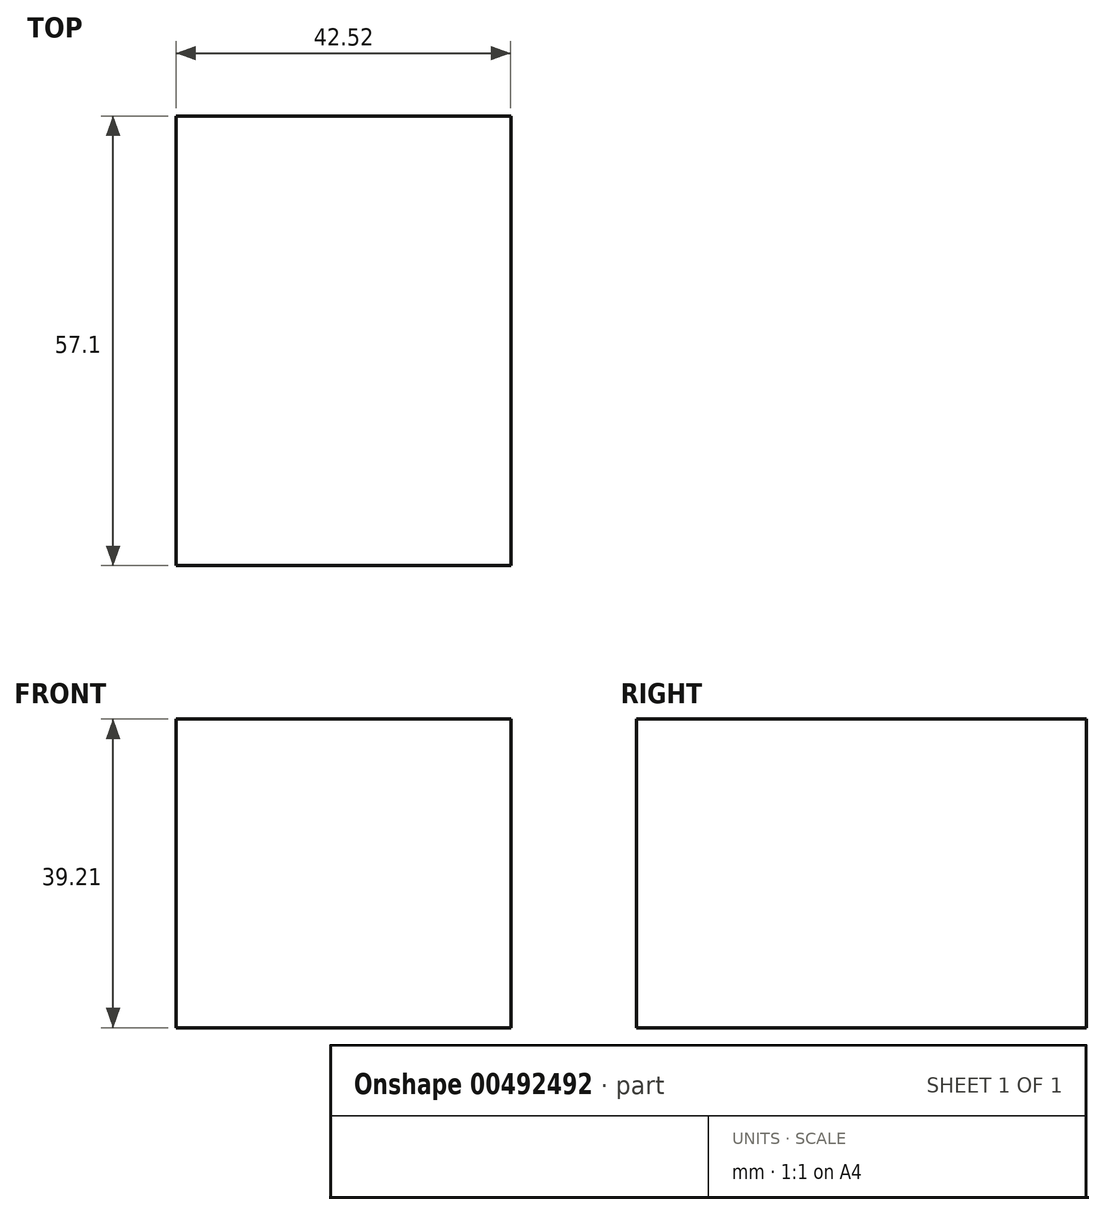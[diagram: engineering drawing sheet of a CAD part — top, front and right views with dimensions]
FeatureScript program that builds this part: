
annotation { "Feature Type Name" : "Feature", "Feature Type Description" : "" }
export const myFeature = defineFeature(function(context is Context, id is Id, definition is map)
    precondition{}
    {
        {
            var Q0;
            Q0=qCreatedBy(makeId("Front.planeOp"),FACE);
            var sketch = newSketch(context, id + "F0", { "sketchPlane" : qUnion([Q0])});
            skLineSegment(sketch, "E0.bottom", {"start": v(-138.9, 9.33) * mm, "end": v(-96.39, 9.33) * mm});
            skLineSegment(sketch, "E0.top", {"start": v(-138.9, 48.54) * mm, "end": v(-96.39, 48.54) * mm});
            skLineSegment(sketch, "E0.left", {"start": v(-138.9, 9.33) * mm, "end": v(-138.9, 48.54) * mm});
            skLineSegment(sketch, "E0.right", {"start": v(-96.39, 9.33) * mm, "end": v(-96.39, 48.54) * mm});
            skPoint(sketch, "E0.middle", {"position": v(-117.65, 28.94) * mm});
            skSolve(sketch);
        }
        {
            var Q0;
            Q0=makeQuery(id+"F0.imprint","IMPRINT",FACE,{"disambiguationData":[TD([[makeQuery(id+"F0.imprint","IMPRINT",EDGE,{"derivedFrom":sQuery(id+"F0.wireOp",EDGE,"E0.bottom")}),1.0]])]});
            extrude(context, id + "F1", {"entities" : qUnion([Q0]), "depth" : 57.1 * mm});
        }
    });
